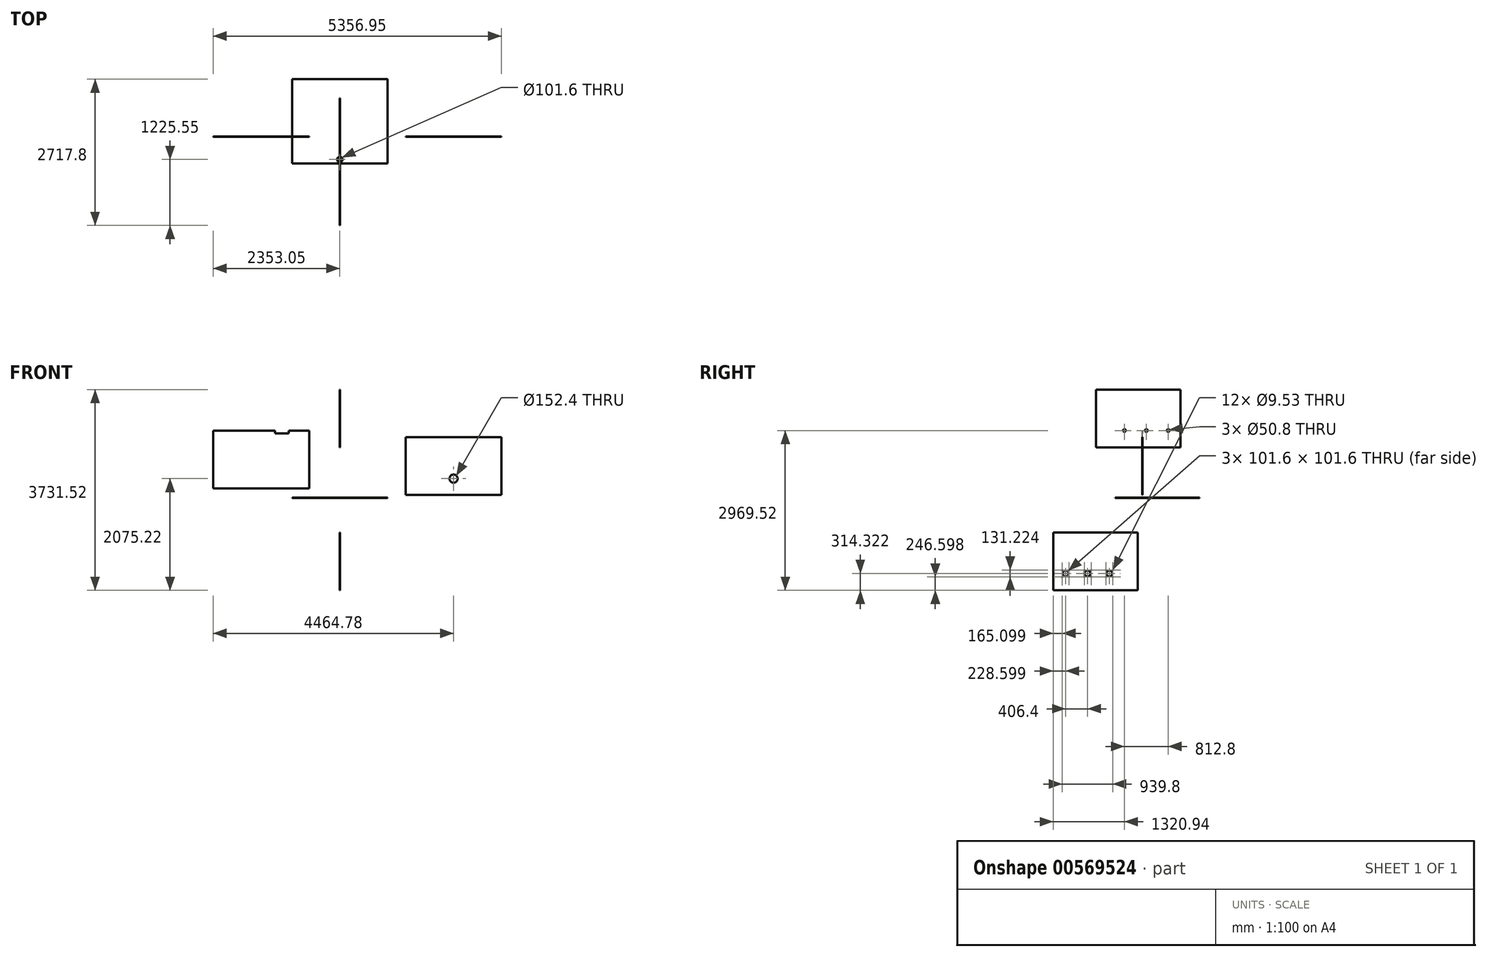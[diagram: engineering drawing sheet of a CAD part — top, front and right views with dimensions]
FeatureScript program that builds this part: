
annotation { "Feature Type Name" : "Feature", "Feature Type Description" : "" }
export const myFeature = defineFeature(function(context is Context, id is Id, definition is map)
    precondition{}
    {
        {
            var Q0;
            Q0=qCreatedBy(makeId("Top.planeOp"),FACE);
            var sketch = newSketch(context, id + "F0", { "sketchPlane" : qUnion([Q0])});
            skLineSegment(sketch, "E0.bottom", {"start": v(-885.83, -505.86) * mm, "end": v(885.82, -505.86) * mm});
            skLineSegment(sketch, "E0.top", {"start": v(-885.83, 1062.6) * mm, "end": v(885.82, 1062.6) * mm});
            skLineSegment(sketch, "E0.left", {"start": v(-885.83, -505.86) * mm, "end": v(-885.83, 1062.6) * mm});
            skLineSegment(sketch, "E0.right", {"start": v(885.83, -505.86) * mm, "end": v(885.82, 1062.6) * mm});
            skCircle(sketch, "E1", {"center": v(0, -429.66) * mm, "radius": 50.8 * mm});
            skSolve(sketch);
        }
        {
            var Q0;
            Q0=qCreatedBy(makeId("Right.planeOp"),FACE);
            var sketch = newSketch(context, id + "F1", { "sketchPlane" : qUnion([Q0])});
            skLineSegment(sketch, "E2.bottom", {"start": v(707.13, 940.17) * mm, "end": v(-861.32, 940.17) * mm});
            skLineSegment(sketch, "E2.top", {"start": v(707.13, 2016.5) * mm, "end": v(-861.32, 2016.5) * mm});
            skLineSegment(sketch, "E2.left", {"start": v(707.13, 940.17) * mm, "end": v(707.13, 2016.5) * mm});
            skLineSegment(sketch, "E2.right", {"start": v(-861.32, 940.17) * mm, "end": v(-861.32, 2016.5) * mm});
            skCircle(sketch, "E3", {"center": v(478.53, 1254.5) * mm, "radius": 25.4 * mm});
            skCircle(sketch, "E4", {"center": v(72.13, 1254.5) * mm, "radius": 25.4 * mm});
            skCircle(sketch, "E5", {"center": v(-334.27, 1254.5) * mm, "radius": 25.4 * mm});
            skSolve(sketch);
        }
        {
            var Q0;
            Q0=qCreatedBy(makeId("Right.planeOp"),FACE);
            var sketch = newSketch(context, id + "F2", { "sketchPlane" : qUnion([Q0])});
            skLineSegment(sketch, "E6.bottom", {"start": v(-1655.21, -1715.03) * mm, "end": v(-86.76, -1715.03) * mm});
            skLineSegment(sketch, "E6.top", {"start": v(-1655.21, -638.7) * mm, "end": v(-86.76, -638.7) * mm});
            skLineSegment(sketch, "E6.left", {"start": v(-1655.21, -1715.03) * mm, "end": v(-1655.21, -638.7) * mm});
            skLineSegment(sketch, "E6.right", {"start": v(-86.76, -1715.03) * mm, "end": v(-86.76, -638.7) * mm});
            skLineSegment(sketch, "E7.bottom", {"start": v(-1477.41, -1451.5) * mm, "end": v(-1375.81, -1451.5) * mm});
            skLineSegment(sketch, "E7.top", {"start": v(-1477.41, -1349.9) * mm, "end": v(-1375.81, -1349.9) * mm});
            skLineSegment(sketch, "E7.left", {"start": v(-1477.41, -1451.5) * mm, "end": v(-1477.41, -1349.9) * mm});
            skLineSegment(sketch, "E7.right", {"start": v(-1375.81, -1451.5) * mm, "end": v(-1375.81, -1349.9) * mm});
            skLineSegment(sketch, "E8.bottom", {"start": v(-1071.01, -1349.9) * mm, "end": v(-969.41, -1349.9) * mm});
            skLineSegment(sketch, "E8.top", {"start": v(-1071.01, -1451.5) * mm, "end": v(-969.41, -1451.5) * mm});
            skLineSegment(sketch, "E8.left", {"start": v(-1071.01, -1349.9) * mm, "end": v(-1071.01, -1451.5) * mm});
            skLineSegment(sketch, "E8.right", {"start": v(-969.41, -1349.9) * mm, "end": v(-969.41, -1451.5) * mm});
            skLineSegment(sketch, "E9.bottom", {"start": v(-664.61, -1349.9) * mm, "end": v(-563.01, -1349.9) * mm});
            skLineSegment(sketch, "E9.top", {"start": v(-664.61, -1451.5) * mm, "end": v(-563.01, -1451.5) * mm});
            skLineSegment(sketch, "E9.left", {"start": v(-664.61, -1349.9) * mm, "end": v(-664.61, -1451.5) * mm});
            skLineSegment(sketch, "E9.right", {"start": v(-563.01, -1349.9) * mm, "end": v(-563.01, -1451.5) * mm});
            skCircle(sketch, "E10", {"center": v(-1363.11, -1337.2) * mm, "radius": 4.76 * mm});
            skCircle(sketch, "E11", {"center": v(-1490.11, -1468.43) * mm, "radius": 4.76 * mm});
            skCircle(sketch, "E12", {"center": v(-1490.11, -1341.43) * mm, "radius": 4.76 * mm});
            skCircle(sketch, "E13", {"center": v(-1363.11, -1464.2) * mm, "radius": 4.76 * mm});
            skCircle(sketch, "E14", {"center": v(-1078.95, -1337.2) * mm, "radius": 4.76 * mm});
            skCircle(sketch, "E15", {"center": v(-951.95, -1337.2) * mm, "radius": 4.76 * mm});
            skCircle(sketch, "E16", {"center": v(-951.95, -1464.2) * mm, "radius": 4.76 * mm});
            skCircle(sketch, "E17", {"center": v(-1078.95, -1464.2) * mm, "radius": 4.76 * mm});
            skCircle(sketch, "E18", {"center": v(-677.31, -1337.2) * mm, "radius": 4.76 * mm});
            skCircle(sketch, "E19", {"center": v(-550.31, -1337.2) * mm, "radius": 4.76 * mm});
            skCircle(sketch, "E20", {"center": v(-550.31, -1464.2) * mm, "radius": 4.76 * mm});
            skCircle(sketch, "E21", {"center": v(-677.31, -1464.2) * mm, "radius": 4.76 * mm});
            skSolve(sketch);
        }
        {
            var Q0;
            Q0=qCreatedBy(makeId("Front.planeOp"),FACE);
            var sketch = newSketch(context, id + "F3", { "sketchPlane" : qUnion([Q0])});
            skLineSegment(sketch, "E22.bottom", {"start": v(-2353.05, 176.56) * mm, "end": v(-568.7, 176.56) * mm});
            skLineSegment(sketch, "E22.top", {"start": v(-2353.05, 1252.88) * mm, "end": v(-568.7, 1252.88) * mm});
            skLineSegment(sketch, "E22.left", {"start": v(-2353.05, 176.56) * mm, "end": v(-2353.05, 1252.88) * mm});
            skLineSegment(sketch, "E22.right", {"start": v(-568.7, 176.56) * mm, "end": v(-568.7, 1252.88) * mm});
            skLineSegment(sketch, "E23.bottom", {"start": v(-1203.7, 1252.88) * mm, "end": v(-949.7, 1252.88) * mm});
            skLineSegment(sketch, "E23.top", {"start": v(-1203.7, 1202.08) * mm, "end": v(-949.7, 1202.08) * mm});
            skLineSegment(sketch, "E23.left", {"start": v(-1203.7, 1252.88) * mm, "end": v(-1203.7, 1202.08) * mm});
            skLineSegment(sketch, "E23.right", {"start": v(-949.7, 1252.88) * mm, "end": v(-949.7, 1202.08) * mm});
            skSolve(sketch);
        }
        {
            var Q0;
            Q0=qCreatedBy(makeId("Front.planeOp"),FACE);
            var sketch = newSketch(context, id + "F4", { "sketchPlane" : qUnion([Q0])});
            skLineSegment(sketch, "E24.bottom", {"start": v(1219.55, 55.39) * mm, "end": v(3003.9, 55.39) * mm});
            skLineSegment(sketch, "E24.top", {"start": v(1219.55, 1131.71) * mm, "end": v(3003.9, 1131.71) * mm});
            skLineSegment(sketch, "E24.left", {"start": v(1219.55, 55.39) * mm, "end": v(1219.55, 1131.71) * mm});
            skLineSegment(sketch, "E24.right", {"start": v(3003.9, 55.39) * mm, "end": v(3003.9, 1131.71) * mm});
            skCircle(sketch, "E25", {"center": v(2111.73, 360.19) * mm, "radius": 76.2 * mm});
            skSolve(sketch);
        }
        {
            var Q0;
            Q0=makeQuery(id+"F3.imprint","IMPRINT",FACE,{"disambiguationData":[TD([[makeQuery(id+"F3.imprint","IMPRINT",EDGE,{"derivedFrom":sQuery(id+"F3.wireOp",EDGE,"E22.bottom")}),1.0]])]});
            extrude(context, id + "F5", {"entities" : qUnion([Q0]), "depth" : 6.35 * mm, "offsetDistance" : 25.4 * mm});
        }
        {
            var Q0;
            Q0=makeQuery(id+"F4.imprint","IMPRINT",FACE,{"disambiguationData":[TD([[makeQuery(id+"F4.imprint","IMPRINT",EDGE,{"derivedFrom":sQuery(id+"F4.wireOp",EDGE,"E24.bottom")}),1.0]])]});
            extrude(context, id + "F6", {"entities" : qUnion([Q0]), "depth" : 6.35 * mm, "offsetDistance" : 25.4 * mm});
        }
        {
            var Q0;
            Q0=makeQuery(id+"F1.imprint","IMPRINT",FACE,{"disambiguationData":[TD([[makeQuery(id+"F1.imprint","IMPRINT",EDGE,{"derivedFrom":sQuery(id+"F1.wireOp",EDGE,"E2.bottom")}),-1.0]])]});
            extrude(context, id + "F7", {"entities" : qUnion([Q0]), "depth" : 6.35 * mm, "offsetDistance" : 25.4 * mm});
        }
        {
            var Q0;
            Q0=makeQuery(id+"F0.imprint","IMPRINT",FACE,{"disambiguationData":[TD([[makeQuery(id+"F0.imprint","IMPRINT",EDGE,{"derivedFrom":sQuery(id+"F0.wireOp",EDGE,"E0.bottom")}),1.0]])]});
            extrude(context, id + "F8", {"entities" : qUnion([Q0]), "depth" : 6.35 * mm, "offsetDistance" : 25.4 * mm});
        }
        {
            var Q0;
            Q0=makeQuery(id+"F2.imprint","IMPRINT",FACE,{"disambiguationData":[TD([[makeQuery(id+"F2.imprint","IMPRINT",EDGE,{"derivedFrom":sQuery(id+"F2.wireOp",EDGE,"E6.bottom")}),1.0]])]});
            extrude(context, id + "F9", {"entities" : qUnion([Q0]), "depth" : 6.35 * mm, "offsetDistance" : 25.4 * mm});
        }
    });
